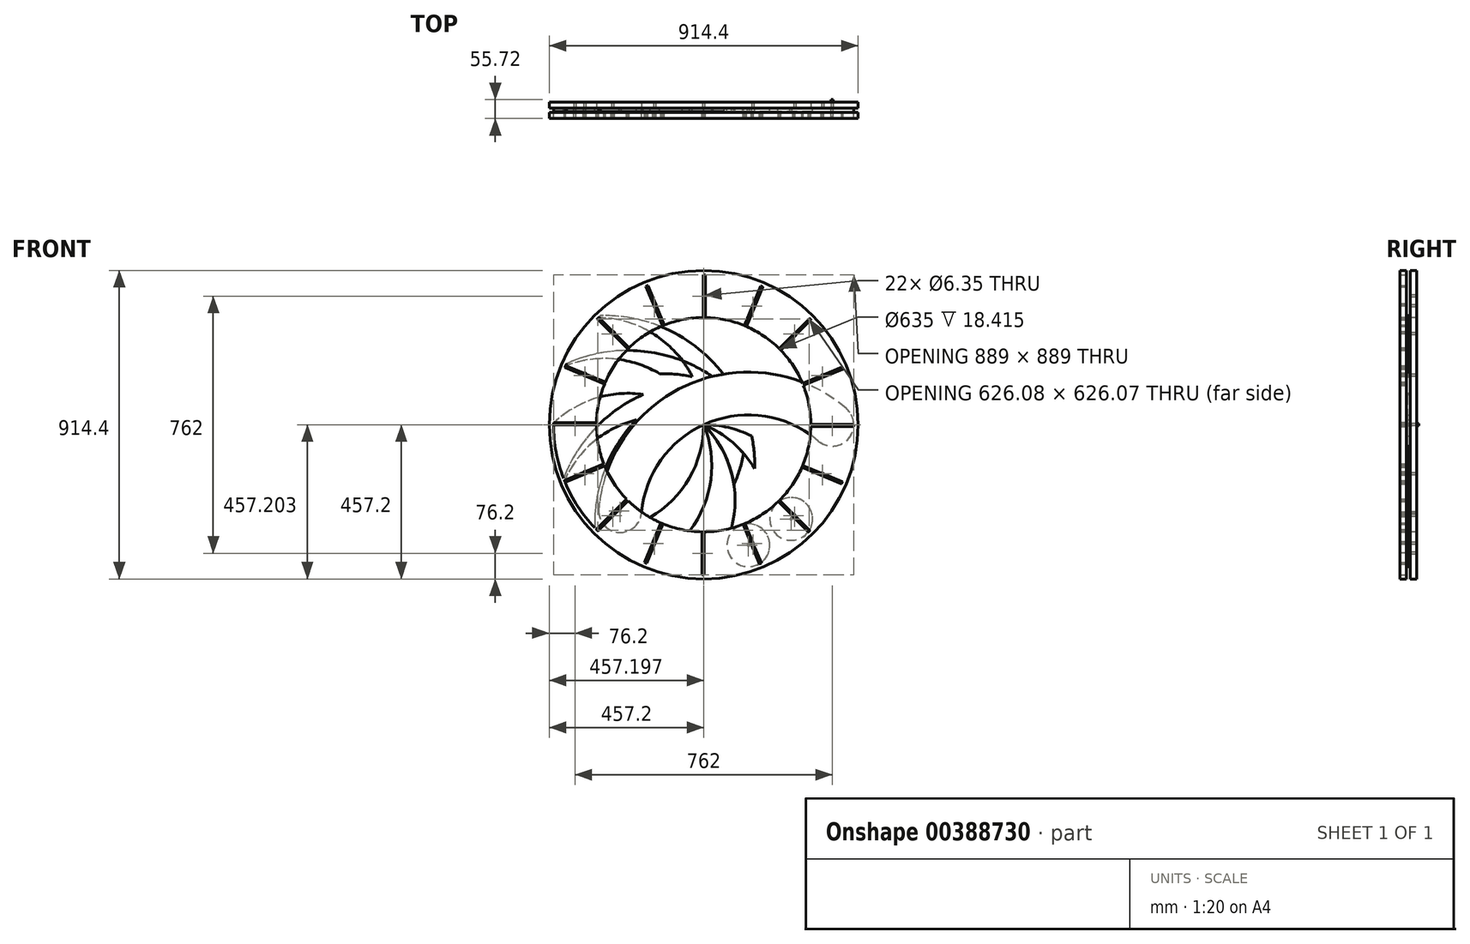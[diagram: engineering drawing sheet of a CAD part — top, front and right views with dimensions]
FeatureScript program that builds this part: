
annotation { "Feature Type Name" : "Feature", "Feature Type Description" : "" }
export const myFeature = defineFeature(function(context is Context, id is Id, definition is map)
    precondition{}
    {
        {
            var Q0;
            Q0=qCreatedBy(makeId("Front.planeOp"),FACE);
            var sketch = newSketch(context, id + "F0", { "sketchPlane" : qUnion([Q0])});
            skCircle(sketch, "E0", {"center": v(0, 0) * mm, "radius": 444.5 * mm});
            skCircle(sketch, "E1", {"center": v(0, 0) * mm, "radius": 457.2 * mm});
            skCircle(sketch, "E2", {"center": v(0, 0) * mm, "radius": 317.5 * mm});
            skCircle(sketch, "E3", {"center": v(0, 0) * mm, "radius": 381 * mm, "construction": true});
            skArc(sketch, "E4", {"start": v(339.55, -48.1) * mm, "mid": v(429.1, -41.45) * mm, "end": v(422.45, 48.1) * mm});
            skArc(sketch, "E5", {"start": v(339.55, -48.1) * mm, "mid": v(12.56, 5.43) * mm, "end": v(-184.03, -261.29) * mm});
            skArc(sketch, "E6", {"start": v(-310.56, -250.35) * mm, "mid": v(-251.54, -319.18) * mm, "end": v(-183.87, -258.84) * mm});
            skArc(sketch, "E7.trimOffspring", {"start": v(422.45, 48.1) * mm, "mid": v(-35.33, 123.06) * mm, "end": v(-310.56, -250.35) * mm});
            skLineSegment(sketch, "E8", {"start": v(0, 0) * mm, "end": v(776.4, 0) * mm, "construction": true});
            skCircle(sketch, "E9", {"center": v(381, 0) * mm, "radius": 3.18 * mm});
            skCircle(sketch, "E10", {"center": v(-247.3, -255.82) * mm, "radius": 3.17 * mm});
            skCircle(sketch, "E11.1.0", {"center": v(352, 145.8) * mm, "radius": 3.18 * mm});
            skCircle(sketch, "E11.2.0", {"center": v(269.4, 269.4) * mm, "radius": 3.18 * mm});
            skCircle(sketch, "E11.3.0", {"center": v(145.8, 352) * mm, "radius": 3.18 * mm});
            skCircle(sketch, "E11.4.0", {"center": v(0, 381) * mm, "radius": 3.18 * mm});
            skCircle(sketch, "E11.5.0", {"center": v(-145.8, 352) * mm, "radius": 3.18 * mm});
            skCircle(sketch, "E11.6.0", {"center": v(-269.4, 269.4) * mm, "radius": 3.18 * mm});
            skCircle(sketch, "E11.7.0", {"center": v(-352, 145.8) * mm, "radius": 3.18 * mm});
            skCircle(sketch, "E11.8.0", {"center": v(-381, 0) * mm, "radius": 3.18 * mm});
            skCircle(sketch, "E11.9.0", {"center": v(-352, -145.8) * mm, "radius": 3.18 * mm});
            skCircle(sketch, "E11.10.0", {"center": v(-269.4, -269.4) * mm, "radius": 3.18 * mm});
            skCircle(sketch, "E11.11.0", {"center": v(-145.8, -352) * mm, "radius": 3.18 * mm});
            skCircle(sketch, "E11.12.0", {"center": v(0, -381) * mm, "radius": 3.18 * mm});
            skCircle(sketch, "E11.13.0", {"center": v(145.8, -352) * mm, "radius": 3.18 * mm});
            skCircle(sketch, "E11.14.0", {"center": v(269.4, -269.4) * mm, "radius": 3.18 * mm});
            skCircle(sketch, "E11.15.0", {"center": v(352, -145.8) * mm, "radius": 3.18 * mm});
            skSolve(sketch);
        }
        {
            var Q0;
            {var subQ3=sQuery(id+"F0.wireOp",EDGE,"E0");Q0=makeQuery(id+"F0.imprint","IMPRINT",FACE,{"disambiguationData":[TD([[makeQuery(id+"F0.imprint","IMPRINT",EDGE,{"derivedFrom":subQ3}),1.0]])]});}
            var Q1;
            Q1=makeQuery(id+"F0.imprint","IMPRINT",FACE,{"disambiguationData":[TD([[makeQuery(id+"F0.imprint","IMPRINT",EDGE,{"derivedFrom":sQuery(id+"F0.wireOp",EDGE,"E9")}),-1.0]])]});
            var Q2;
            Q2=makeQuery(id+"F0.imprint","IMPRINT",FACE,{"disambiguationData":[TD([[makeQuery(id+"F0.imprint","IMPRINT",EDGE,{"derivedFrom":sQuery(id+"F0.wireOp",EDGE,"E10")}),-1.0]])]});
            var Q3;
            Q3=makeQuery(id+"F0.imprint","IMPRINT",FACE,{"disambiguationData":[TD([[makeQuery(id+"F0.imprint","IMPRINT",EDGE,{"derivedFrom":sQuery(id+"F0.wireOp",EDGE,"E10")}),1.0]])]});
            var Q4;
            Q4=makeQuery(id+"F0.imprint","IMPRINT",FACE,{"disambiguationData":[TD([[makeQuery(id+"F0.imprint","IMPRINT",EDGE,{"derivedFrom":sQuery(id+"F0.wireOp",EDGE,"E0")}),-1.0]])]});
            extrude(context, id + "F1", {"entities" : qUnion([Q0, Q1, Q2, Q3, Q4]), "oppositeDirection" : true, "depth" : 18.41 * mm});
        }
        {
            var Q0;
            {var subQ1=sQuery(id+"F0.wireOp",EDGE,"E2");var subQ6=makeQuery(id+"F0.imprint","INTERSECT",VERTEX,{"derivedFrom":[subQ1,sQuery(id+"F0.wireOp",EDGE,"E6")]});Q0=makeQuery(id+"F0.imprint","IMPRINT",FACE,{"disambiguationData":[TD([[makeQuery(id+"F0.imprint","IMPRINT",EDGE,{"disambiguationData":[TD([[subQ6,1.0]])],"derivedFrom":subQ1}),1.0]])]});}
            var Q1;
            Q1=makeQuery(id+"F0.imprint","IMPRINT",FACE,{"disambiguationData":[TD([[makeQuery(id+"F0.imprint","IMPRINT",EDGE,{"derivedFrom":sQuery(id+"F0.wireOp",EDGE,"E9")}),-1.0]])]});
            var Q2;
            Q2=makeQuery(id+"F0.imprint","IMPRINT",FACE,{"disambiguationData":[TD([[makeQuery(id+"F0.imprint","IMPRINT",EDGE,{"derivedFrom":sQuery(id+"F0.wireOp",EDGE,"E10")}),-1.0]])]});
            var Q3;
            Q3=makeQuery(id+"F0.imprint","IMPRINT",FACE,{"disambiguationData":[TD([[makeQuery(id+"F0.imprint","IMPRINT",EDGE,{"derivedFrom":sQuery(id+"F0.wireOp",EDGE,"E11.10.0")}),1.0]])]});
            extrude(context, id + "F2", {"entities" : qUnion([Q0, Q1, Q2, Q3]), "depth" : 11.9 * mm});
        }
        {
            var Q0;
            Q0=qCreatedBy(makeId("Front.planeOp"),FACE);
            var sketch = newSketch(context, id + "F3", { "sketchPlane" : qUnion([Q0])});
            skCircle(sketch, "E12", {"center": v(0, 0) * mm, "radius": 444.5 * mm});
            skCircle(sketch, "E13", {"center": v(0, 0) * mm, "radius": 457.2 * mm});
            skCircle(sketch, "E14", {"center": v(0, 0) * mm, "radius": 317.5 * mm});
            skCircle(sketch, "E15", {"center": v(0, 0) * mm, "radius": 381 * mm, "construction": true});
            skArc(sketch, "E16", {"start": v(339.55, -48.1) * mm, "mid": v(429.1, -41.45) * mm, "end": v(422.45, 48.1) * mm});
            skArc(sketch, "E17", {"start": v(339.55, -48.1) * mm, "mid": v(12.56, 5.43) * mm, "end": v(-184.03, -261.29) * mm});
            skArc(sketch, "E18", {"start": v(-310.56, -250.35) * mm, "mid": v(-251.54, -319.18) * mm, "end": v(-183.87, -258.84) * mm});
            skArc(sketch, "E19.trimOffspring", {"start": v(422.45, 48.1) * mm, "mid": v(-35.33, 123.06) * mm, "end": v(-310.56, -250.35) * mm});
            skLineSegment(sketch, "E20", {"start": v(0, 0) * mm, "end": v(776.4, 0) * mm, "construction": true});
            skCircle(sketch, "E21", {"center": v(381, 0) * mm, "radius": 3.18 * mm});
            skCircle(sketch, "E22", {"center": v(-247.3, -255.82) * mm, "radius": 3.17 * mm});
            skCircle(sketch, "E23.1.0", {"center": v(352.88, 145.98) * mm, "radius": 3.18 * mm});
            skCircle(sketch, "E23.2.0", {"center": v(271.03, 270.1) * mm, "radius": 3.18 * mm});
            skCircle(sketch, "E23.3.0", {"center": v(147.91, 353.43) * mm, "radius": 3.18 * mm});
            skCircle(sketch, "E23.4.0", {"center": v(2.28, 383.31) * mm, "radius": 3.18 * mm});
            skCircle(sketch, "E23.5.0", {"center": v(-143.7, 355.19) * mm, "radius": 3.18 * mm});
            skCircle(sketch, "E23.6.0", {"center": v(-267.8, 273.34) * mm, "radius": 3.18 * mm});
            skCircle(sketch, "E23.7.0", {"center": v(-351.15, 150.23) * mm, "radius": 3.18 * mm});
            skCircle(sketch, "E23.8.0", {"center": v(-381.03, 4.6) * mm, "radius": 3.18 * mm});
            skCircle(sketch, "E23.9.0", {"center": v(-352.9, -141.4) * mm, "radius": 3.18 * mm});
            skCircle(sketch, "E23.10.0", {"center": v(-271.06, -265.5) * mm, "radius": 3.18 * mm});
            skCircle(sketch, "E23.11.0", {"center": v(-147.94, -348.84) * mm, "radius": 3.18 * mm});
            skCircle(sketch, "E23.12.0", {"center": v(-2.31, -378.72) * mm, "radius": 3.18 * mm});
            skCircle(sketch, "E23.13.0", {"center": v(143.67, -350.6) * mm, "radius": 3.18 * mm});
            skCircle(sketch, "E23.14.0", {"center": v(267.78, -268.75) * mm, "radius": 3.18 * mm});
            skCircle(sketch, "E23.15.0", {"center": v(351.12, -145.63) * mm, "radius": 3.18 * mm});
            skPoint(sketch, "E23.center", {"position": v(-0.01, 2.3) * mm});
            skLineSegment(sketch, "E24.left", {"start": v(5.46, 317.45) * mm, "end": v(5.46, 444.47) * mm});
            skLineSegment(sketch, "E24.right", {"start": v(-0.9, 317.45) * mm, "end": v(-0.9, 444.5) * mm});
            skPoint(sketch, "E24.top.start.orphan", {"position": v(5.46, 449.17) * mm});
            skPoint(sketch, "E25.orphan", {"position": v(-0.9, 449.17) * mm});
            skPoint(sketch, "E24.bottom.start.orphan", {"position": v(5.46, 317.45) * mm});
            skLineSegment(sketch, "E26.1.0", {"start": v(-116.44, 295.38) * mm, "end": v(-165.05, 412.72) * mm});
            skLineSegment(sketch, "E26.1.1", {"start": v(-122.3, 292.95) * mm, "end": v(-170.93, 410.32) * mm});
            skLineSegment(sketch, "E26.2.0", {"start": v(-220.61, 228.33) * mm, "end": v(-310.43, 318.14) * mm});
            skLineSegment(sketch, "E26.2.1", {"start": v(-225.1, 223.84) * mm, "end": v(-314.94, 313.68) * mm});
            skLineSegment(sketch, "E26.3.0", {"start": v(-291.2, 126.53) * mm, "end": v(-408.55, 175.13) * mm});
            skLineSegment(sketch, "E26.3.1", {"start": v(-293.63, 120.66) * mm, "end": v(-411, 169.28) * mm});
            skLineSegment(sketch, "E26.4.0", {"start": v(-317.45, 5.46) * mm, "end": v(-444.47, 5.46) * mm});
            skLineSegment(sketch, "E26.4.1", {"start": v(-317.45, -0.9) * mm, "end": v(-444.5, -0.9) * mm});
            skLineSegment(sketch, "E26.5.0", {"start": v(-295.38, -116.44) * mm, "end": v(-412.72, -165.05) * mm});
            skLineSegment(sketch, "E26.5.1", {"start": v(-292.95, -122.3) * mm, "end": v(-410.32, -170.93) * mm});
            skLineSegment(sketch, "E26.6.0", {"start": v(-228.33, -220.61) * mm, "end": v(-318.14, -310.43) * mm});
            skLineSegment(sketch, "E26.6.1", {"start": v(-223.84, -225.1) * mm, "end": v(-313.68, -314.94) * mm});
            skLineSegment(sketch, "E26.7.0", {"start": v(-126.53, -291.2) * mm, "end": v(-175.13, -408.55) * mm});
            skLineSegment(sketch, "E26.7.1", {"start": v(-120.66, -293.63) * mm, "end": v(-169.28, -411) * mm});
            skLineSegment(sketch, "E26.8.0", {"start": v(-5.46, -317.45) * mm, "end": v(-5.46, -444.47) * mm});
            skLineSegment(sketch, "E26.8.1", {"start": v(0.9, -317.45) * mm, "end": v(0.9, -444.5) * mm});
            skLineSegment(sketch, "E26.9.0", {"start": v(116.44, -295.38) * mm, "end": v(165.05, -412.72) * mm});
            skLineSegment(sketch, "E26.9.1", {"start": v(122.3, -292.95) * mm, "end": v(170.93, -410.32) * mm});
            skLineSegment(sketch, "E26.10.0", {"start": v(220.61, -228.33) * mm, "end": v(310.43, -318.14) * mm});
            skLineSegment(sketch, "E26.10.1", {"start": v(225.1, -223.84) * mm, "end": v(314.94, -313.68) * mm});
            skLineSegment(sketch, "E26.11.0", {"start": v(291.2, -126.53) * mm, "end": v(408.55, -175.13) * mm});
            skLineSegment(sketch, "E26.11.1", {"start": v(293.63, -120.66) * mm, "end": v(411, -169.28) * mm});
            skLineSegment(sketch, "E26.12.0", {"start": v(317.45, -5.46) * mm, "end": v(444.47, -5.46) * mm});
            skLineSegment(sketch, "E26.12.1", {"start": v(317.45, 0.9) * mm, "end": v(444.5, 0.9) * mm});
            skLineSegment(sketch, "E26.13.0", {"start": v(295.38, 116.44) * mm, "end": v(412.72, 165.05) * mm});
            skLineSegment(sketch, "E26.13.1", {"start": v(292.95, 122.3) * mm, "end": v(410.32, 170.93) * mm});
            skLineSegment(sketch, "E26.14.0", {"start": v(228.33, 220.61) * mm, "end": v(318.14, 310.43) * mm});
            skLineSegment(sketch, "E26.14.1", {"start": v(223.84, 225.1) * mm, "end": v(313.68, 314.94) * mm});
            skLineSegment(sketch, "E26.15.0", {"start": v(126.53, 291.2) * mm, "end": v(175.13, 408.55) * mm});
            skLineSegment(sketch, "E26.15.1", {"start": v(120.66, 293.63) * mm, "end": v(169.28, 411) * mm});
            skSolve(sketch);
        }
        {
            var Q0;
            Q0 = qSketchRegion(id + "F3", true);
            var Q1;
            {var subQ8=sQuery(id+"F3.wireOp",EDGE,"E26.15.0");Q1=makeQuery(id+"F3.imprint","IMPRINT",FACE,{"disambiguationData":[TD([[makeQuery(id+"F3.imprint","IMPRINT",EDGE,{"derivedFrom":subQ8}),-1.0]])]});}
            var Q2;
            {var subQ0=sQuery(id+"F3.wireOp",EDGE,"E24.left");var subQ1=sQuery(id+"F3.wireOp",EDGE,"E14");var subQ2=makeQuery(id+"F3.imprint","INTERSECT",VERTEX,{"derivedFrom":[subQ1,subQ0]});Q2=makeQuery(id+"F3.imprint","IMPRINT",FACE,{"disambiguationData":[TD([[makeQuery(id+"F3.imprint","IMPRINT",EDGE,{"disambiguationData":[TD([[subQ2,1.0]])],"derivedFrom":subQ1}),-1.0]])]});}
            var Q3;
            {var subQ1=sQuery(id+"F3.wireOp",EDGE,"E14");var subQ6=sQuery(id+"F3.wireOp",EDGE,"E26.1.0");var subQ10=makeQuery(id+"F3.imprint","INTERSECT",VERTEX,{"derivedFrom":[subQ1,subQ6]});Q3=makeQuery(id+"F3.imprint","IMPRINT",FACE,{"disambiguationData":[TD([[makeQuery(id+"F3.imprint","IMPRINT",EDGE,{"disambiguationData":[TD([[subQ10,1.0]])],"derivedFrom":subQ1}),-1.0]])]});}
            var Q4;
            {var subQ0=sQuery(id+"F3.wireOp",EDGE,"E26.2.0");var subQ1=sQuery(id+"F3.wireOp",EDGE,"E14");var subQ2=makeQuery(id+"F3.imprint","INTERSECT",VERTEX,{"derivedFrom":[subQ1,subQ0]});Q4=makeQuery(id+"F3.imprint","IMPRINT",FACE,{"disambiguationData":[TD([[makeQuery(id+"F3.imprint","IMPRINT",EDGE,{"disambiguationData":[TD([[subQ2,1.0]])],"derivedFrom":subQ1}),-1.0]])]});}
            var Q5;
            {var subQ3=sQuery(id+"F3.wireOp",EDGE,"E14");var subQ5=sQuery(id+"F3.wireOp",EDGE,"E26.3.0");var subQ6=makeQuery(id+"F3.imprint","INTERSECT",VERTEX,{"derivedFrom":[subQ3,subQ5]});Q5=makeQuery(id+"F3.imprint","IMPRINT",FACE,{"disambiguationData":[TD([[makeQuery(id+"F3.imprint","IMPRINT",EDGE,{"disambiguationData":[TD([[subQ6,1.0]])],"derivedFrom":subQ3}),-1.0]])]});}
            var Q6;
            {var subQ3=sQuery(id+"F3.wireOp",EDGE,"E14");var subQ5=sQuery(id+"F3.wireOp",EDGE,"E26.5.1");var subQ6=makeQuery(id+"F3.imprint","INTERSECT",VERTEX,{"derivedFrom":[subQ3,subQ5]});Q6=makeQuery(id+"F3.imprint","IMPRINT",FACE,{"disambiguationData":[TD([[makeQuery(id+"F3.imprint","IMPRINT",EDGE,{"disambiguationData":[TD([[subQ6,-1.0]])],"derivedFrom":subQ3}),-1.0]])]});}
            var Q7;
            {var subQ0=sQuery(id+"F3.wireOp",EDGE,"E26.3.0");var subQ1=sQuery(id+"F3.wireOp",EDGE,"E23.7.0");var subQ2=makeQuery(id+"F3.imprint","INTERSECT",VERTEX,{"disambiguationData":[OD(0.0)],"derivedFrom":[subQ1,subQ0]});Q7=makeQuery(id+"F3.imprint","IMPRINT",FACE,{"disambiguationData":[TD([[makeQuery(id+"F3.imprint","IMPRINT",EDGE,{"disambiguationData":[TD([[subQ2,-1.0]])],"derivedFrom":subQ1}),1.0]])]});}
            var Q8;
            {var subQ0=sQuery(id+"F3.wireOp",EDGE,"E26.2.0");var subQ1=sQuery(id+"F3.wireOp",EDGE,"E23.6.0");var subQ2=makeQuery(id+"F3.imprint","INTERSECT",VERTEX,{"disambiguationData":[OD(0.0)],"derivedFrom":[subQ1,subQ0]});Q8=makeQuery(id+"F3.imprint","IMPRINT",FACE,{"disambiguationData":[TD([[makeQuery(id+"F3.imprint","IMPRINT",EDGE,{"disambiguationData":[TD([[subQ2,-1.0]])],"derivedFrom":subQ1}),1.0]])]});}
            var Q9;
            {var subQ0=sQuery(id+"F3.wireOp",EDGE,"E26.15.1");var subQ1=sQuery(id+"F3.wireOp",EDGE,"E23.3.0");var subQ2=makeQuery(id+"F3.imprint","INTERSECT",VERTEX,{"disambiguationData":[OD(0.0)],"derivedFrom":[subQ1,subQ0]});Q9=makeQuery(id+"F3.imprint","IMPRINT",FACE,{"disambiguationData":[TD([[makeQuery(id+"F3.imprint","IMPRINT",EDGE,{"disambiguationData":[TD([[subQ2,1.0]])],"derivedFrom":subQ1}),1.0]])]});}
            var Q10;
            {var subQ8=sQuery(id+"F3.wireOp",EDGE,"E26.14.0");Q10=makeQuery(id+"F3.imprint","IMPRINT",FACE,{"disambiguationData":[TD([[makeQuery(id+"F3.imprint","IMPRINT",EDGE,{"derivedFrom":subQ8}),-1.0]])]});}
            var Q11;
            {var subQ0=sQuery(id+"F3.wireOp",EDGE,"E26.14.1");var subQ1=sQuery(id+"F3.wireOp",EDGE,"E23.2.0");var subQ2=makeQuery(id+"F3.imprint","INTERSECT",VERTEX,{"disambiguationData":[OD(0.0)],"derivedFrom":[subQ1,subQ0]});Q11=makeQuery(id+"F3.imprint","IMPRINT",FACE,{"disambiguationData":[TD([[makeQuery(id+"F3.imprint","IMPRINT",EDGE,{"disambiguationData":[TD([[subQ2,1.0]])],"derivedFrom":subQ1}),1.0]])]});}
            var Q12;
            {var subQ3=sQuery(id+"F3.wireOp",EDGE,"E16");var subQ7=sQuery(id+"F3.wireOp",EDGE,"E19.trimOffspring");var subQ9=makeQuery(id+"F3.imprint","INTERSECT",VERTEX,{"derivedFrom":[subQ3,subQ7]});Q12=makeQuery(id+"F3.imprint","IMPRINT",FACE,{"disambiguationData":[TD([[makeQuery(id+"F3.imprint","IMPRINT",EDGE,{"disambiguationData":[TD([[subQ9,1.0]])],"derivedFrom":subQ3}),-1.0]])]});}
            var Q13;
            {var subQ0=sQuery(id+"F3.wireOp",EDGE,"E26.13.1");var subQ1=sQuery(id+"F3.wireOp",EDGE,"E23.1.0");var subQ2=makeQuery(id+"F3.imprint","INTERSECT",VERTEX,{"disambiguationData":[OD(0.0)],"derivedFrom":[subQ1,subQ0]});Q13=makeQuery(id+"F3.imprint","IMPRINT",FACE,{"disambiguationData":[TD([[makeQuery(id+"F3.imprint","IMPRINT",EDGE,{"disambiguationData":[TD([[subQ2,1.0]])],"derivedFrom":subQ1}),1.0]])]});}
            var Q14;
            {var subQ0=sQuery(id+"F3.wireOp",EDGE,"E26.13.1");var subQ1=sQuery(id+"F3.wireOp",EDGE,"E14");var subQ2=makeQuery(id+"F3.imprint","INTERSECT",VERTEX,{"derivedFrom":[subQ1,subQ0]});Q14=makeQuery(id+"F3.imprint","IMPRINT",FACE,{"disambiguationData":[TD([[makeQuery(id+"F3.imprint","IMPRINT",EDGE,{"disambiguationData":[TD([[subQ2,-1.0]])],"derivedFrom":subQ1}),-1.0]])]});}
            var Q15;
            {var subQ7=sQuery(id+"F3.wireOp",EDGE,"E26.13.0");var subQ10=sQuery(id+"F3.wireOp",EDGE,"E14");var subQ11=makeQuery(id+"F3.imprint","INTERSECT",VERTEX,{"derivedFrom":[subQ10,subQ7]});Q15=makeQuery(id+"F3.imprint","IMPRINT",FACE,{"disambiguationData":[TD([[makeQuery(id+"F3.imprint","IMPRINT",EDGE,{"disambiguationData":[TD([[subQ11,1.0]])],"derivedFrom":subQ10}),-1.0]])]});}
            var Q16;
            {var subQ0=sQuery(id+"F3.wireOp",EDGE,"E26.12.0");var subQ1=sQuery(id+"F3.wireOp",EDGE,"E14");var subQ2=makeQuery(id+"F3.imprint","INTERSECT",VERTEX,{"derivedFrom":[subQ1,subQ0]});Q16=makeQuery(id+"F3.imprint","IMPRINT",FACE,{"disambiguationData":[TD([[makeQuery(id+"F3.imprint","IMPRINT",EDGE,{"disambiguationData":[TD([[subQ2,1.0]])],"derivedFrom":subQ1}),-1.0]])]});}
            var Q17;
            {var subQ0=sQuery(id+"F3.wireOp",EDGE,"E26.12.1");var subQ1=sQuery(id+"F3.wireOp",EDGE,"E21");var subQ2=makeQuery(id+"F3.imprint","INTERSECT",VERTEX,{"disambiguationData":[OD(0.0)],"derivedFrom":[subQ1,subQ0]});Q17=makeQuery(id+"F3.imprint","IMPRINT",FACE,{"disambiguationData":[TD([[makeQuery(id+"F3.imprint","IMPRINT",EDGE,{"disambiguationData":[TD([[subQ2,1.0]])],"derivedFrom":subQ1}),1.0]])]});}
            var Q18;
            {var subQ3=sQuery(id+"F3.wireOp",EDGE,"E14");var subQ7=sQuery(id+"F3.wireOp",EDGE,"E26.11.1");var subQ11=makeQuery(id+"F3.imprint","INTERSECT",VERTEX,{"derivedFrom":[subQ3,subQ7]});Q18=makeQuery(id+"F3.imprint","IMPRINT",FACE,{"disambiguationData":[TD([[makeQuery(id+"F3.imprint","IMPRINT",EDGE,{"disambiguationData":[TD([[subQ11,-1.0]])],"derivedFrom":subQ3}),-1.0]])]});}
            var Q19;
            {var subQ5=sQuery(id+"F3.wireOp",EDGE,"E26.11.0");Q19=makeQuery(id+"F3.imprint","IMPRINT",FACE,{"disambiguationData":[TD([[makeQuery(id+"F3.imprint","IMPRINT",EDGE,{"derivedFrom":subQ5}),-1.0]])]});}
            var Q20;
            {var subQ0=sQuery(id+"F3.wireOp",EDGE,"E26.11.1");var subQ1=sQuery(id+"F3.wireOp",EDGE,"E23.15.0");var subQ2=makeQuery(id+"F3.imprint","INTERSECT",VERTEX,{"disambiguationData":[OD(0.0)],"derivedFrom":[subQ1,subQ0]});Q20=makeQuery(id+"F3.imprint","IMPRINT",FACE,{"disambiguationData":[TD([[makeQuery(id+"F3.imprint","IMPRINT",EDGE,{"disambiguationData":[TD([[subQ2,1.0]])],"derivedFrom":subQ1}),1.0]])]});}
            var Q21;
            {var subQ8=sQuery(id+"F3.wireOp",EDGE,"E26.10.0");Q21=makeQuery(id+"F3.imprint","IMPRINT",FACE,{"disambiguationData":[TD([[makeQuery(id+"F3.imprint","IMPRINT",EDGE,{"derivedFrom":subQ8}),-1.0]])]});}
            var Q22;
            {var subQ0=sQuery(id+"F3.wireOp",EDGE,"E26.10.1");var subQ1=sQuery(id+"F3.wireOp",EDGE,"E23.14.0");var subQ2=makeQuery(id+"F3.imprint","INTERSECT",VERTEX,{"disambiguationData":[OD(0.0)],"derivedFrom":[subQ1,subQ0]});Q22=makeQuery(id+"F3.imprint","IMPRINT",FACE,{"disambiguationData":[TD([[makeQuery(id+"F3.imprint","IMPRINT",EDGE,{"disambiguationData":[TD([[subQ2,1.0]])],"derivedFrom":subQ1}),1.0]])]});}
            var Q23;
            {var subQ0=sQuery(id+"F3.wireOp",EDGE,"E26.9.0");Q23=makeQuery(id+"F3.imprint","IMPRINT",FACE,{"disambiguationData":[TD([[makeQuery(id+"F3.imprint","IMPRINT",EDGE,{"derivedFrom":subQ0}),-1.0]])]});}
            var Q24;
            {var subQ0=sQuery(id+"F3.wireOp",EDGE,"E26.9.1");var subQ1=sQuery(id+"F3.wireOp",EDGE,"E23.13.0");var subQ2=makeQuery(id+"F3.imprint","INTERSECT",VERTEX,{"disambiguationData":[OD(0.0)],"derivedFrom":[subQ1,subQ0]});Q24=makeQuery(id+"F3.imprint","IMPRINT",FACE,{"disambiguationData":[TD([[makeQuery(id+"F3.imprint","IMPRINT",EDGE,{"disambiguationData":[TD([[subQ2,1.0]])],"derivedFrom":subQ1}),1.0]])]});}
            var Q25;
            {var subQ0=sQuery(id+"F3.wireOp",EDGE,"E26.8.0");var subQ1=sQuery(id+"F3.wireOp",EDGE,"E14");var subQ2=makeQuery(id+"F3.imprint","INTERSECT",VERTEX,{"derivedFrom":[subQ1,subQ0]});Q25=makeQuery(id+"F3.imprint","IMPRINT",FACE,{"disambiguationData":[TD([[makeQuery(id+"F3.imprint","IMPRINT",EDGE,{"disambiguationData":[TD([[subQ2,1.0]])],"derivedFrom":subQ1}),-1.0]])]});}
            var Q26;
            {var subQ0=sQuery(id+"F3.wireOp",EDGE,"E26.7.0");var subQ7=sQuery(id+"F3.wireOp",EDGE,"E14");var subQ11=makeQuery(id+"F3.imprint","INTERSECT",VERTEX,{"derivedFrom":[subQ7,subQ0]});Q26=makeQuery(id+"F3.imprint","IMPRINT",FACE,{"disambiguationData":[TD([[makeQuery(id+"F3.imprint","IMPRINT",EDGE,{"disambiguationData":[TD([[subQ11,1.0]])],"derivedFrom":subQ7}),-1.0]])]});}
            var Q27;
            {var subQ0=sQuery(id+"F3.wireOp",EDGE,"E26.7.0");var subQ1=sQuery(id+"F3.wireOp",EDGE,"E23.11.0");var subQ2=makeQuery(id+"F3.imprint","INTERSECT",VERTEX,{"disambiguationData":[OD(0.0)],"derivedFrom":[subQ1,subQ0]});Q27=makeQuery(id+"F3.imprint","IMPRINT",FACE,{"disambiguationData":[TD([[makeQuery(id+"F3.imprint","IMPRINT",EDGE,{"disambiguationData":[TD([[subQ2,-1.0]])],"derivedFrom":subQ1}),1.0]])]});}
            var Q28;
            Q28=makeQuery(id+"F3.imprint","IMPRINT",FACE,{"disambiguationData":[TD([[makeQuery(id+"F3.imprint","IMPRINT",EDGE,{"derivedFrom":sQuery(id+"F3.wireOp",EDGE,"E22")}),-1.0]])]});
            var Q29;
            {var subQ3=sQuery(id+"F3.wireOp",EDGE,"E14");var subQ5=sQuery(id+"F3.wireOp",EDGE,"E26.6.0");var subQ10=makeQuery(id+"F3.imprint","INTERSECT",VERTEX,{"derivedFrom":[subQ3,subQ5]});Q29=makeQuery(id+"F3.imprint","IMPRINT",FACE,{"disambiguationData":[TD([[makeQuery(id+"F3.imprint","IMPRINT",EDGE,{"disambiguationData":[TD([[subQ10,1.0]])],"derivedFrom":subQ3}),-1.0]])]});}
            var Q30;
            Q30=makeQuery(id+"F3.imprint","IMPRINT",FACE,{"disambiguationData":[TD([[makeQuery(id+"F3.imprint","IMPRINT",EDGE,{"derivedFrom":sQuery(id+"F3.wireOp",EDGE,"E22")}),1.0]])]});
            var Q31;
            {var subQ0=sQuery(id+"F3.wireOp",EDGE,"E26.6.0");var subQ1=sQuery(id+"F3.wireOp",EDGE,"E23.10.0");var subQ2=makeQuery(id+"F3.imprint","INTERSECT",VERTEX,{"disambiguationData":[OD(0.0)],"derivedFrom":[subQ1,subQ0]});Q31=makeQuery(id+"F3.imprint","IMPRINT",FACE,{"disambiguationData":[TD([[makeQuery(id+"F3.imprint","IMPRINT",EDGE,{"disambiguationData":[TD([[subQ2,-1.0]])],"derivedFrom":subQ1}),1.0]])]});}
            var Q32;
            {var subQ0=sQuery(id+"F3.wireOp",EDGE,"E26.5.0");var subQ1=sQuery(id+"F3.wireOp",EDGE,"E14");var subQ2=makeQuery(id+"F3.imprint","INTERSECT",VERTEX,{"derivedFrom":[subQ1,subQ0]});Q32=makeQuery(id+"F3.imprint","IMPRINT",FACE,{"disambiguationData":[TD([[makeQuery(id+"F3.imprint","IMPRINT",EDGE,{"disambiguationData":[TD([[subQ2,1.0]])],"derivedFrom":subQ1}),-1.0]])]});}
            var Q33;
            {var subQ0=sQuery(id+"F3.wireOp",EDGE,"E26.4.0");var subQ1=sQuery(id+"F3.wireOp",EDGE,"E14");var subQ2=makeQuery(id+"F3.imprint","INTERSECT",VERTEX,{"derivedFrom":[subQ1,subQ0]});Q33=makeQuery(id+"F3.imprint","IMPRINT",FACE,{"disambiguationData":[TD([[makeQuery(id+"F3.imprint","IMPRINT",EDGE,{"disambiguationData":[TD([[subQ2,1.0]])],"derivedFrom":subQ1}),-1.0]])]});}
            var Q34;
            {var subQ0=sQuery(id+"F3.wireOp",EDGE,"E26.5.0");var subQ1=sQuery(id+"F3.wireOp",EDGE,"E23.9.0");var subQ2=makeQuery(id+"F3.imprint","INTERSECT",VERTEX,{"disambiguationData":[OD(0.0)],"derivedFrom":[subQ1,subQ0]});Q34=makeQuery(id+"F3.imprint","IMPRINT",FACE,{"disambiguationData":[TD([[makeQuery(id+"F3.imprint","IMPRINT",EDGE,{"disambiguationData":[TD([[subQ2,-1.0]])],"derivedFrom":subQ1}),1.0]])]});}
            var Q35;
            {var subQ0=sQuery(id+"F3.wireOp",EDGE,"E26.4.0");var subQ1=sQuery(id+"F3.wireOp",EDGE,"E23.8.0");var subQ2=makeQuery(id+"F3.imprint","INTERSECT",VERTEX,{"disambiguationData":[OD(0.0)],"derivedFrom":[subQ1,subQ0]});Q35=makeQuery(id+"F3.imprint","IMPRINT",FACE,{"disambiguationData":[TD([[makeQuery(id+"F3.imprint","IMPRINT",EDGE,{"disambiguationData":[TD([[subQ2,-1.0]])],"derivedFrom":subQ1}),1.0]])]});}
            var Q36;
            {var subQ0=sQuery(id+"F3.wireOp",EDGE,"E26.1.0");var subQ1=sQuery(id+"F3.wireOp",EDGE,"E23.5.0");var subQ2=makeQuery(id+"F3.imprint","INTERSECT",VERTEX,{"disambiguationData":[OD(0.0)],"derivedFrom":[subQ1,subQ0]});Q36=makeQuery(id+"F3.imprint","IMPRINT",FACE,{"disambiguationData":[TD([[makeQuery(id+"F3.imprint","IMPRINT",EDGE,{"disambiguationData":[TD([[subQ2,-1.0]])],"derivedFrom":subQ1}),1.0]])]});}
            extrude(context, id + "F4", {"entities" : qUnion([Q0, Q1, Q2, Q3, Q4, Q5, Q6, Q7, Q8, Q9, Q10, Q11, Q12, Q13, Q14, Q15, Q16, Q17, Q18, Q19, Q20, Q21, Q22, Q23, Q24, Q25, Q26, Q27, Q28, Q29, Q30, Q31, Q32, Q33, Q34, Q35, Q36]), "depth" : 30.32 * mm, "hasSecondDirection" : true, "secondDirectionOppositeDirection" : false, "secondDirectionDepth" : 11.9 * mm});
        }
        {
            var Q0;
            Q0=qCreatedBy(makeId("Front.planeOp"),FACE);
            var sketch = newSketch(context, id + "F5", { "sketchPlane" : qUnion([Q0])});
            skCircle(sketch, "E27", {"center": v(0, 0) * mm, "radius": 444.5 * mm});
            skCircle(sketch, "E28", {"center": v(0, 0) * mm, "radius": 457.2 * mm});
            skCircle(sketch, "E29", {"center": v(0, 0) * mm, "radius": 317.5 * mm});
            skCircle(sketch, "E30", {"center": v(0, 0) * mm, "radius": 381 * mm, "construction": true});
            skLineSegment(sketch, "E31", {"start": v(-384.18, 0) * mm, "end": v(776.4, 0) * mm, "construction": true});
            skCircle(sketch, "E32", {"center": v(381, 0) * mm, "radius": 3.18 * mm});
            skCircle(sketch, "E33.1.0", {"center": v(352, 145.8) * mm, "radius": 3.18 * mm});
            skCircle(sketch, "E33.2.0", {"center": v(269.4, 269.4) * mm, "radius": 3.18 * mm});
            skCircle(sketch, "E33.3.0", {"center": v(145.8, 352) * mm, "radius": 3.18 * mm});
            skCircle(sketch, "E33.4.0", {"center": v(0, 381) * mm, "radius": 3.18 * mm});
            skCircle(sketch, "E33.5.0", {"center": v(-145.8, 352) * mm, "radius": 3.18 * mm});
            skCircle(sketch, "E33.6.0", {"center": v(-269.4, 269.4) * mm, "radius": 3.18 * mm});
            skCircle(sketch, "E33.7.0", {"center": v(-352, 145.8) * mm, "radius": 3.18 * mm});
            skCircle(sketch, "E33.8.0", {"center": v(-381, 0) * mm, "radius": 3.18 * mm});
            skCircle(sketch, "E33.9.0", {"center": v(-352, -145.8) * mm, "radius": 3.18 * mm});
            skCircle(sketch, "E33.10.0", {"center": v(-269.4, -269.4) * mm, "radius": 3.18 * mm});
            skCircle(sketch, "E33.11.0", {"center": v(-145.8, -352) * mm, "radius": 3.18 * mm});
            skCircle(sketch, "E33.12.0", {"center": v(0, -381) * mm, "radius": 3.18 * mm});
            skCircle(sketch, "E33.13.0", {"center": v(145.8, -352) * mm, "radius": 3.18 * mm});
            skCircle(sketch, "E33.14.0", {"center": v(269.4, -269.4) * mm, "radius": 3.18 * mm});
            skCircle(sketch, "E33.15.0", {"center": v(352, -145.8) * mm, "radius": 3.18 * mm});
            skLineSegment(sketch, "E34", {"start": v(-352, 145.8) * mm, "end": v(352, -145.8) * mm, "construction": true});
            skLineSegment(sketch, "E35", {"start": v(269.4, -269.4) * mm, "end": v(-269.4, 269.4) * mm, "construction": true});
            skLineSegment(sketch, "E36", {"start": v(-145.8, 352) * mm, "end": v(145.8, -352) * mm, "construction": true});
            skLineSegment(sketch, "E37", {"start": v(0, -381) * mm, "end": v(0, 381) * mm, "construction": true});
            skLineSegment(sketch, "E38", {"start": v(-145.8, -352) * mm, "end": v(145.8, 352) * mm, "construction": true});
            skLineSegment(sketch, "E39", {"start": v(-269.4, -269.4) * mm, "end": v(269.4, 269.4) * mm, "construction": true});
            skLineSegment(sketch, "E40", {"start": v(352, 145.8) * mm, "end": v(-352, -145.8) * mm, "construction": true});
            skCircle(sketch, "E41", {"center": v(121.5, -293.33) * mm, "radius": 317.5 * mm});
            skCircle(sketch, "E42", {"center": v(121.5, -293.33) * mm, "radius": 444.5 * mm});
            skCircle(sketch, "E43", {"center": v(0, -317.5) * mm, "radius": 317.5 * mm});
            skCircle(sketch, "E44", {"center": v(0, -317.5) * mm, "radius": 444.5 * mm});
            skCircle(sketch, "E45", {"center": v(-121.5, -293.33) * mm, "radius": 317.5 * mm});
            skCircle(sketch, "E46", {"center": v(-121.5, -293.33) * mm, "radius": 444.5 * mm});
            skCircle(sketch, "E47", {"center": v(-224.5, -224.5) * mm, "radius": 317.5 * mm});
            skCircle(sketch, "E48", {"center": v(-224.5, -224.5) * mm, "radius": 444.5 * mm});
            skCircle(sketch, "E49", {"center": v(-293.33, -121.5) * mm, "radius": 317.5 * mm});
            skCircle(sketch, "E50", {"center": v(-293.33, -121.5) * mm, "radius": 444.5 * mm});
            skCircle(sketch, "E51", {"center": v(-317.5, 0) * mm, "radius": 317.5 * mm});
            skCircle(sketch, "E52", {"center": v(-317.5, 0) * mm, "radius": 444.5 * mm});
            skCircle(sketch, "E53", {"center": v(-224.5, -224.5) * mm, "radius": 381 * mm, "construction": true});
            skCircle(sketch, "E54", {"center": v(132.65, -357.16) * mm, "radius": 63.5 * mm});
            skCircle(sketch, "E55", {"center": v(132.65, -357.16) * mm, "radius": 3.18 * mm});
            skCircle(sketch, "E56", {"center": v(-121.5, -293.33) * mm, "radius": 381 * mm, "construction": true});
            skCircle(sketch, "E57", {"center": v(259.24, -279.2) * mm, "radius": 63.5 * mm});
            skCircle(sketch, "E58", {"center": v(259.11, -279.32) * mm, "radius": 3.18 * mm});
            skSolve(sketch);
        }
        {
            var Q0;
            Q0=makeQuery(id+"F5.imprint","IMPRINT",FACE,{"disambiguationData":[TD([[makeQuery(id+"F5.imprint","IMPRINT",EDGE,{"derivedFrom":sQuery(id+"F5.wireOp",EDGE,"E33.13.0")}),-1.0]])]});
            var Q1;
            Q1=makeQuery(id+"F5.imprint","IMPRINT",FACE,{"disambiguationData":[TD([[makeQuery(id+"F5.imprint","IMPRINT",EDGE,{"derivedFrom":sQuery(id+"F5.wireOp",EDGE,"E33.13.0")}),1.0]])]});
            var Q2;
            {var subQ0=sQuery(id+"F5.wireOp",EDGE,"E54");var subQ1=sQuery(id+"F5.wireOp",EDGE,"E50");var subQ2=makeQuery(id+"F5.imprint","INTERSECT",VERTEX,{"disambiguationData":[OD(0.0)],"derivedFrom":[subQ1,subQ0]});Q2=makeQuery(id+"F5.imprint","IMPRINT",FACE,{"disambiguationData":[TD([[makeQuery(id+"F5.imprint","IMPRINT",EDGE,{"disambiguationData":[TD([[subQ2,-1.0]])],"derivedFrom":subQ1}),1.0]])]});}
            var Q3;
            {var subQ0=sQuery(id+"F5.wireOp",EDGE,"E54");var subQ1=sQuery(id+"F5.wireOp",EDGE,"E45");var subQ2=makeQuery(id+"F5.imprint","INTERSECT",VERTEX,{"disambiguationData":[OD(0.0)],"derivedFrom":[subQ1,subQ0]});Q3=makeQuery(id+"F5.imprint","IMPRINT",FACE,{"disambiguationData":[TD([[makeQuery(id+"F5.imprint","IMPRINT",EDGE,{"disambiguationData":[TD([[subQ2,-1.0]])],"derivedFrom":subQ1}),-1.0]])]});}
            var Q4;
            {var subQ0=sQuery(id+"F5.wireOp",EDGE,"E50");var subQ1=sQuery(id+"F5.wireOp",EDGE,"E29");var subQ2=makeQuery(id+"F5.imprint","INTERSECT",VERTEX,{"disambiguationData":[OD(1.0)],"derivedFrom":[subQ1,subQ0]});Q4=makeQuery(id+"F5.imprint","IMPRINT",FACE,{"disambiguationData":[TD([[makeQuery(id+"F5.imprint","IMPRINT",EDGE,{"disambiguationData":[TD([[subQ2,-1.0]])],"derivedFrom":subQ1}),-1.0]])]});}
            var Q5;
            {var subQ0=sQuery(id+"F5.wireOp",EDGE,"E50");var subQ1=sQuery(id+"F5.wireOp",EDGE,"E29");var subQ2=makeQuery(id+"F5.imprint","INTERSECT",VERTEX,{"disambiguationData":[OD(1.0)],"derivedFrom":[subQ1,subQ0]});Q5=makeQuery(id+"F5.imprint","IMPRINT",FACE,{"disambiguationData":[TD([[makeQuery(id+"F5.imprint","IMPRINT",EDGE,{"disambiguationData":[TD([[subQ2,-1.0]])],"derivedFrom":subQ1}),1.0]])]});}
            var Q6;
            {var subQ0=sQuery(id+"F5.wireOp",EDGE,"E47");var subQ1=sQuery(id+"F5.wireOp",EDGE,"E29");var subQ2=makeQuery(id+"F5.imprint","INTERSECT",VERTEX,{"disambiguationData":[OD(1.0)],"derivedFrom":[subQ1,subQ0]});Q6=makeQuery(id+"F5.imprint","IMPRINT",FACE,{"disambiguationData":[TD([[makeQuery(id+"F5.imprint","IMPRINT",EDGE,{"disambiguationData":[TD([[subQ2,-1.0]])],"derivedFrom":subQ1}),1.0]])]});}
            var Q7;
            {var subQ0=sQuery(id+"F5.wireOp",EDGE,"E47");var subQ1=sQuery(id+"F5.wireOp",EDGE,"E29");var subQ2=makeQuery(id+"F5.imprint","INTERSECT",VERTEX,{"disambiguationData":[OD(1.0)],"derivedFrom":[subQ1,subQ0]});Q7=makeQuery(id+"F5.imprint","IMPRINT",FACE,{"disambiguationData":[TD([[makeQuery(id+"F5.imprint","IMPRINT",EDGE,{"disambiguationData":[TD([[subQ2,-1.0]])],"derivedFrom":subQ1}),-1.0]])]});}
            var Q8;
            {var subQ0=sQuery(id+"F5.wireOp",EDGE,"E52");var subQ1=sQuery(id+"F5.wireOp",EDGE,"E45");var subQ2=makeQuery(id+"F5.imprint","INTERSECT",VERTEX,{"disambiguationData":[OD(0.0)],"derivedFrom":[subQ1,subQ0]});Q8=makeQuery(id+"F5.imprint","IMPRINT",FACE,{"disambiguationData":[TD([[makeQuery(id+"F5.imprint","IMPRINT",EDGE,{"disambiguationData":[TD([[subQ2,1.0]])],"derivedFrom":subQ0}),1.0]])]});}
            var Q9;
            {var subQ0=sQuery(id+"F5.wireOp",EDGE,"E54");var subQ1=sQuery(id+"F5.wireOp",EDGE,"E29");var subQ2=makeQuery(id+"F5.imprint","INTERSECT",VERTEX,{"derivedFrom":[subQ1,subQ0]});Q9=makeQuery(id+"F5.imprint","IMPRINT",FACE,{"disambiguationData":[TD([[makeQuery(id+"F5.imprint","IMPRINT",EDGE,{"disambiguationData":[TD([[subQ2,-1.0]])],"derivedFrom":subQ1}),-1.0]])]});}
            extrude(context, id + "F6", {"entities" : qUnion([Q0, Q1, Q2, Q3, Q4, Q5, Q6, Q7, Q8, Q9]), "depth" : 9.52 * mm});
        }
        {
            var Q0;
            Q0=makeQuery(id+"F5.imprint","IMPRINT",FACE,{"disambiguationData":[TD([[makeQuery(id+"F5.imprint","IMPRINT",EDGE,{"derivedFrom":sQuery(id+"F5.wireOp",EDGE,"E33.14.0")}),-1.0]])]});
            var Q1;
            {var subQ0=sQuery(id+"F5.wireOp",EDGE,"E57");var subQ1=sQuery(id+"F5.wireOp",EDGE,"E48");var subQ2=makeQuery(id+"F5.imprint","INTERSECT",VERTEX,{"disambiguationData":[OD(0.0)],"derivedFrom":[subQ1,subQ0]});Q1=makeQuery(id+"F5.imprint","IMPRINT",FACE,{"disambiguationData":[TD([[makeQuery(id+"F5.imprint","IMPRINT",EDGE,{"disambiguationData":[TD([[subQ2,-1.0]])],"derivedFrom":subQ1}),1.0]])]});}
            var Q2;
            {var subQ0=sQuery(id+"F5.wireOp",EDGE,"E57");var subQ1=sQuery(id+"F5.wireOp",EDGE,"E43");var subQ2=makeQuery(id+"F5.imprint","INTERSECT",VERTEX,{"disambiguationData":[OD(0.0)],"derivedFrom":[subQ1,subQ0]});Q2=makeQuery(id+"F5.imprint","IMPRINT",FACE,{"disambiguationData":[TD([[makeQuery(id+"F5.imprint","IMPRINT",EDGE,{"disambiguationData":[TD([[subQ2,-1.0]])],"derivedFrom":subQ1}),-1.0]])]});}
            var Q3;
            Q3=makeQuery(id+"F5.imprint","IMPRINT",FACE,{"disambiguationData":[TD([[makeQuery(id+"F5.imprint","IMPRINT",EDGE,{"derivedFrom":sQuery(id+"F5.wireOp",EDGE,"E33.14.0")}),1.0]])]});
            var Q4;
            {var subQ0=sQuery(id+"F5.wireOp",EDGE,"E45");var subQ1=sQuery(id+"F5.wireOp",EDGE,"E29");var subQ2=makeQuery(id+"F5.imprint","INTERSECT",VERTEX,{"disambiguationData":[OD(1.0)],"derivedFrom":[subQ1,subQ0]});Q4=makeQuery(id+"F5.imprint","IMPRINT",FACE,{"disambiguationData":[TD([[makeQuery(id+"F5.imprint","IMPRINT",EDGE,{"disambiguationData":[TD([[subQ2,-1.0]])],"derivedFrom":subQ1}),-1.0]])]});}
            var Q5;
            {var subQ5=sQuery(id+"F5.wireOp",EDGE,"E29");var subQ8=sQuery(id+"F5.wireOp",EDGE,"E45");var subQ9=makeQuery(id+"F5.imprint","INTERSECT",VERTEX,{"disambiguationData":[OD(1.0)],"derivedFrom":[subQ5,subQ8]});Q5=makeQuery(id+"F5.imprint","IMPRINT",FACE,{"disambiguationData":[TD([[makeQuery(id+"F5.imprint","IMPRINT",EDGE,{"disambiguationData":[TD([[subQ9,-1.0]])],"derivedFrom":subQ5}),1.0]])]});}
            var Q6;
            {var subQ0=sQuery(id+"F5.wireOp",EDGE,"E48");var subQ1=sQuery(id+"F5.wireOp",EDGE,"E29");var subQ2=makeQuery(id+"F5.imprint","INTERSECT",VERTEX,{"disambiguationData":[OD(1.0)],"derivedFrom":[subQ1,subQ0]});Q6=makeQuery(id+"F5.imprint","IMPRINT",FACE,{"disambiguationData":[TD([[makeQuery(id+"F5.imprint","IMPRINT",EDGE,{"disambiguationData":[TD([[subQ2,-1.0]])],"derivedFrom":subQ1}),1.0]])]});}
            var Q7;
            {var subQ0=sQuery(id+"F5.wireOp",EDGE,"E48");var subQ1=sQuery(id+"F5.wireOp",EDGE,"E29");var subQ2=makeQuery(id+"F5.imprint","INTERSECT",VERTEX,{"disambiguationData":[OD(1.0)],"derivedFrom":[subQ1,subQ0]});Q7=makeQuery(id+"F5.imprint","IMPRINT",FACE,{"disambiguationData":[TD([[makeQuery(id+"F5.imprint","IMPRINT",EDGE,{"disambiguationData":[TD([[subQ2,-1.0]])],"derivedFrom":subQ1}),-1.0]])]});}
            var Q8;
            {var subQ0=sQuery(id+"F5.wireOp",EDGE,"E50");var subQ1=sQuery(id+"F5.wireOp",EDGE,"E43");var subQ2=makeQuery(id+"F5.imprint","INTERSECT",VERTEX,{"disambiguationData":[OD(0.0)],"derivedFrom":[subQ1,subQ0]});Q8=makeQuery(id+"F5.imprint","IMPRINT",FACE,{"disambiguationData":[TD([[makeQuery(id+"F5.imprint","IMPRINT",EDGE,{"disambiguationData":[TD([[subQ2,-1.0]])],"derivedFrom":subQ1}),1.0]])]});}
            var Q9;
            {var subQ0=sQuery(id+"F5.wireOp",EDGE,"E52");var subQ1=sQuery(id+"F5.wireOp",EDGE,"E43");var subQ2=makeQuery(id+"F5.imprint","INTERSECT",VERTEX,{"disambiguationData":[OD(0.0)],"derivedFrom":[subQ1,subQ0]});Q9=makeQuery(id+"F5.imprint","IMPRINT",FACE,{"disambiguationData":[TD([[makeQuery(id+"F5.imprint","IMPRINT",EDGE,{"disambiguationData":[TD([[subQ2,1.0]])],"derivedFrom":subQ0}),1.0]])]});}
            var Q10;
            {var subQ0=sQuery(id+"F5.wireOp",EDGE,"E57");var subQ1=sQuery(id+"F5.wireOp",EDGE,"E29");var subQ2=makeQuery(id+"F5.imprint","INTERSECT",VERTEX,{"derivedFrom":[subQ1,subQ0]});Q10=makeQuery(id+"F5.imprint","IMPRINT",FACE,{"disambiguationData":[TD([[makeQuery(id+"F5.imprint","IMPRINT",EDGE,{"disambiguationData":[TD([[subQ2,-1.0]])],"derivedFrom":subQ1}),-1.0]])]});}
            extrude(context, id + "F7", {"entities" : qUnion([Q0, Q1, Q2, Q3, Q4, Q5, Q6, Q7, Q8, Q9, Q10]), "depth" : 9.52 * mm});
        }
        {
            var Q0;
            Q0=makeQuery(id+"F5.imprint","IMPRINT",FACE,{"disambiguationData":[TD([[makeQuery(id+"F5.imprint","IMPRINT",EDGE,{"derivedFrom":sQuery(id+"F5.wireOp",EDGE,"E32")}),1.0]])]});
            extrude(context, id + "F8", {"entities" : qUnion([Q0]), "endBound" : BoundingType.SYMMETRIC, "depth" : 50.8 * mm});
        }
        {
            var Q0;
            {var subQ0=sQuery(id+"F5.wireOp",EDGE,"E51");var subQ1=sQuery(id+"F5.wireOp",EDGE,"E29");var subQ2=makeQuery(id+"F5.imprint","INTERSECT",VERTEX,{"disambiguationData":[OD(1.0)],"derivedFrom":[subQ1,subQ0]});Q0=makeQuery(id+"F5.imprint","IMPRINT",FACE,{"disambiguationData":[TD([[makeQuery(id+"F5.imprint","IMPRINT",EDGE,{"disambiguationData":[TD([[subQ2,-1.0]])],"derivedFrom":subQ1}),1.0]])]});}
            extrude(context, id + "F9", {"entities" : qUnion([Q0]), "depth" : 9.52 * mm});
        }
        {
            var Q0;
            {var subQ0=sQuery(id+"F5.wireOp",EDGE,"E52");var subQ1=sQuery(id+"F5.wireOp",EDGE,"E29");var subQ2=makeQuery(id+"F5.imprint","INTERSECT",VERTEX,{"disambiguationData":[OD(1.0)],"derivedFrom":[subQ1,subQ0]});Q0=makeQuery(id+"F5.imprint","IMPRINT",FACE,{"disambiguationData":[TD([[makeQuery(id+"F5.imprint","IMPRINT",EDGE,{"disambiguationData":[TD([[subQ2,-1.0]])],"derivedFrom":subQ1}),1.0]])]});}
            var Q1;
            {var subQ0=sQuery(id+"F5.wireOp",EDGE,"E49");var subQ1=sQuery(id+"F5.wireOp",EDGE,"E29");var subQ2=makeQuery(id+"F5.imprint","INTERSECT",VERTEX,{"disambiguationData":[OD(1.0)],"derivedFrom":[subQ1,subQ0]});Q1=makeQuery(id+"F5.imprint","IMPRINT",FACE,{"disambiguationData":[TD([[makeQuery(id+"F5.imprint","IMPRINT",EDGE,{"disambiguationData":[TD([[subQ2,-1.0]])],"derivedFrom":subQ1}),1.0]])]});}
            extrude(context, id + "F10", {"entities" : qUnion([Q0, Q1]), "depth" : 9.52 * mm});
        }
    });
